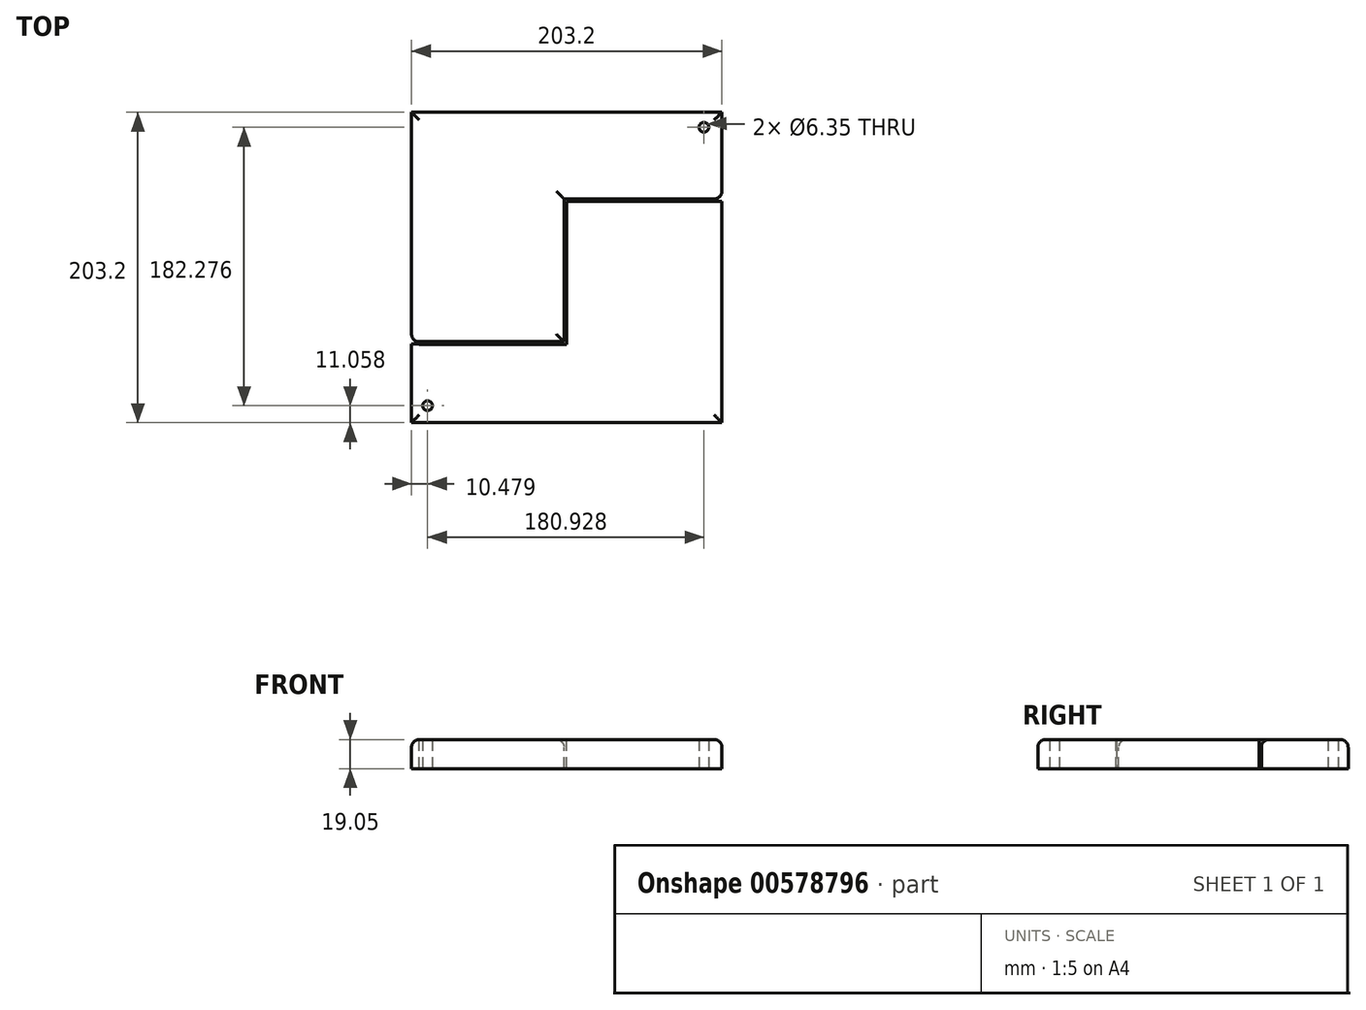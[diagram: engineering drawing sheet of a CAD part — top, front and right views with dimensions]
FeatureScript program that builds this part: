
annotation { "Feature Type Name" : "Feature", "Feature Type Description" : "" }
export const myFeature = defineFeature(function(context is Context, id is Id, definition is map)
    precondition{}
    {
        {
            var Q0;
            Q0=qCreatedBy(makeId("Top.planeOp"),FACE);
            var sketch = newSketch(context, id + "F0", { "sketchPlane" : qUnion([Q0])});
            skLineSegment(sketch, "E0.bottom", {"start": v(-119.21, 139.22) * mm, "end": v(83.99, 139.22) * mm});
            skLineSegment(sketch, "E0.top", {"start": v(-119.21, -63.98) * mm, "end": v(83.99, -63.98) * mm});
            skLineSegment(sketch, "E0.left", {"start": v(-119.21, 139.22) * mm, "end": v(-119.21, -63.98) * mm});
            skLineSegment(sketch, "E0.right", {"start": v(83.99, 139.22) * mm, "end": v(83.99, -63.98) * mm});
            skSolve(sketch);
        }
        {
            var Q0;
            Q0=makeQuery(id+"F0.imprint","IMPRINT",FACE,{"disambiguationData":[TD([[makeQuery(id+"F0.imprint","IMPRINT",EDGE,{"derivedFrom":sQuery(id+"F0.wireOp",EDGE,"E0.bottom")}),-1.0]])]});
            extrude(context, id + "F1", {"entities" : qUnion([Q0]), "depth" : 19.05 * mm, "offsetDistance" : 25.4 * mm});
        }
        {
            var Q0;
            Q0=makeQuery(id+"F1.opExtrude","CAP_FACE",FACE,{"disambiguationData":[OSD([sQuery(id+"F0.wireOp",EDGE,"E0.bottom"),sQuery(id+"F0.wireOp",EDGE,"E0.top"),sQuery(id+"F0.wireOp",EDGE,"E0.left"),sQuery(id+"F0.wireOp",EDGE,"E0.right")])],"isStart":false});
            fillet(context, id + "F2", {"entities" : qUnion([Q0]), "radius" : 5.08 * mm, "tangentPropagation" : true, "allowEdgeOverflow" : false});
        }
        {
            var Q0;
            Q0=makeQuery(id+"F1.opExtrude","CAP_FACE",FACE,{"disambiguationData":[OSD([sQuery(id+"F0.wireOp",EDGE,"E0.bottom"),sQuery(id+"F0.wireOp",EDGE,"E0.top"),sQuery(id+"F0.wireOp",EDGE,"E0.left"),sQuery(id+"F0.wireOp",EDGE,"E0.right")])],"isStart":false});
            var sketch = newSketch(context, id + "F3", { "sketchPlane" : qUnion([Q0])});
            skLineSegment(sketch, "E1", {"start": v(78.9, -58.9) * mm, "end": v(78.9, 80.8) * mm});
            skLineSegment(sketch, "E2", {"start": v(78.9, 80.8) * mm, "end": v(-17.61, 80.8) * mm});
            skPoint(sketch, "E2.endSnap0", {"position": v(-17.61, -58.9) * mm});
            skLineSegment(sketch, "E3", {"start": v(-17.61, 80.8) * mm, "end": v(-17.61, -12.67) * mm});
            skLineSegment(sketch, "E4", {"start": v(-17.61, -12.67) * mm, "end": v(-114.13, -12.67) * mm});
            skLineSegment(sketch, "E5", {"start": v(-114.13, -12.67) * mm, "end": v(-114.13, -11.06) * mm});
            skLineSegment(sketch, "E6", {"start": v(-114.13, -11.06) * mm, "end": v(-19.38, -11.06) * mm});
            skLineSegment(sketch, "E7", {"start": v(-19.38, -11.06) * mm, "end": v(-19.38, 80.8) * mm});
            skLineSegment(sketch, "E8", {"start": v(-19.38, 80.8) * mm, "end": v(-19.38, 82.44) * mm});
            skLineSegment(sketch, "E9", {"start": v(-19.38, 82.44) * mm, "end": v(78.9, 82.44) * mm});
            skLineSegment(sketch, "E10", {"start": v(78.9, 82.44) * mm, "end": v(90.2, 82.44) * mm});
            skLineSegment(sketch, "E11", {"start": v(90.2, 82.44) * mm, "end": v(90.2, 80.8) * mm});
            skLineSegment(sketch, "E12", {"start": v(90.2, 80.8) * mm, "end": v(78.9, 80.8) * mm});
            skLineSegment(sketch, "E13", {"start": v(-114.13, -11.06) * mm, "end": v(-131.84, -11.06) * mm});
            skLineSegment(sketch, "E14", {"start": v(-131.84, -11.06) * mm, "end": v(-131.84, -12.35) * mm});
            skLineSegment(sketch, "E15", {"start": v(-131.84, -12.35) * mm, "end": v(-110, -12.67) * mm});
            skSolve(sketch);
        }
        {
            var Q0;
            Q0 = qSketchRegion(id + "F3", true);
            extrude(context, id + "F4", {"entities" : qUnion([Q0]), "operationType" : NewBodyOperationType.REMOVE, "endBound" : BoundingType.THROUGH_ALL, "oppositeDirection" : true, "depth" : 25.4 * mm, "offsetDistance" : 25.4 * mm});
        }
        {
            var Q0;
            {var subQ0=sQuery(id+"F0.wireOp",EDGE,"E0.right");var subQ1=sQuery(id+"F0.wireOp",EDGE,"E0.left");var subQ2=sQuery(id+"F0.wireOp",EDGE,"E0.bottom");Q0=makeQuery(id+"F4.boolean.opBoolean","SPLIT",FACE,{"disambiguationData":[TD([makeQuery(id+"F2.opFillet","BLEND_FACE",FACE,{"disambiguationData":[OSD([subQ2])]})])],"derivedFrom":makeQuery(id+"F1.opExtrude","CAP_FACE",FACE,{"disambiguationData":[OSD([subQ2,sQuery(id+"F0.wireOp",EDGE,"E0.top"),subQ1,subQ0])],"isStart":false})});}
            var Q1;
            {var subQ0=sQuery(id+"F0.wireOp",EDGE,"E0.right");var subQ1=sQuery(id+"F0.wireOp",EDGE,"E0.left");var subQ2=sQuery(id+"F0.wireOp",EDGE,"E0.top");Q1=makeQuery(id+"F4.boolean.opBoolean","SPLIT",FACE,{"disambiguationData":[TD([makeQuery(id+"F2.opFillet","BLEND_FACE",FACE,{"disambiguationData":[OSD([subQ2])]})])],"derivedFrom":makeQuery(id+"F1.opExtrude","CAP_FACE",FACE,{"disambiguationData":[OSD([sQuery(id+"F0.wireOp",EDGE,"E0.bottom"),subQ2,subQ1,subQ0])],"isStart":false})});}
            fillet(context, id + "F5", {"entities" : qUnion([Q0, Q1]), "radius" : 5.08 * mm, "tangentPropagation" : true, "allowEdgeOverflow" : false});
        }
        {
            var Q0;
            {var subQ0=sQuery(id+"F0.wireOp",EDGE,"E0.right");var subQ1=sQuery(id+"F0.wireOp",EDGE,"E0.left");var subQ2=sQuery(id+"F0.wireOp",EDGE,"E0.top");Q0=makeQuery(id+"F4.boolean.opBoolean","SPLIT",FACE,{"disambiguationData":[TD([makeQuery(id+"F1.opExtrude","SWEPT_FACE",FACE,{"disambiguationData":[OSD([subQ2])]})])],"derivedFrom":makeQuery(id+"F1.opExtrude","CAP_FACE",FACE,{"disambiguationData":[OSD([sQuery(id+"F0.wireOp",EDGE,"E0.bottom"),subQ2,subQ1,subQ0])],"isStart":true})});}
            var sketch = newSketch(context, id + "F6", { "sketchPlane" : qUnion([Q0])});
            skLineSegment(sketch, "E16", {"start": v(-119.21, 63.98) * mm, "end": v(-108.73, 52.92) * mm});
            skCircle(sketch, "E17", {"center": v(-108.73, 52.92) * mm, "radius": 3.18 * mm});
            skLineSegment(sketch, "E18", {"start": v(84.02, -138.98) * mm, "end": v(72.2, -129.35) * mm});
            skCircle(sketch, "E19", {"center": v(72.2, -129.35) * mm, "radius": 3.18 * mm});
            skSolve(sketch);
        }
        {
            var Q0;
            Q0=makeQuery(id+"F6.imprint","IMPRINT",FACE,{"disambiguationData":[TD([[makeQuery(id+"F6.imprint","IMPRINT",EDGE,{"derivedFrom":sQuery(id+"F6.wireOp",EDGE,"E17")}),1.0]])]});
            var Q1;
            Q1=makeQuery(id+"F6.imprint","IMPRINT",FACE,{"disambiguationData":[TD([[makeQuery(id+"F6.imprint","IMPRINT",EDGE,{"derivedFrom":sQuery(id+"F6.wireOp",EDGE,"E19")}),1.0]])]});
            extrude(context, id + "F7", {"entities" : qUnion([Q0, Q1]), "operationType" : NewBodyOperationType.REMOVE, "endBound" : BoundingType.THROUGH_ALL, "oppositeDirection" : true, "depth" : 25.4 * mm, "offsetDistance" : 25.4 * mm});
        }
        {
            var Q0;
            Q0 = qSketchRegion(id + "F6", true);
            extrude(context, id + "F8", {"entities" : qUnion([Q0]), "operationType" : NewBodyOperationType.REMOVE, "endBound" : BoundingType.THROUGH_ALL, "oppositeDirection" : true, "depth" : 25.4 * mm, "offsetDistance" : 25.4 * mm});
        }
    });
